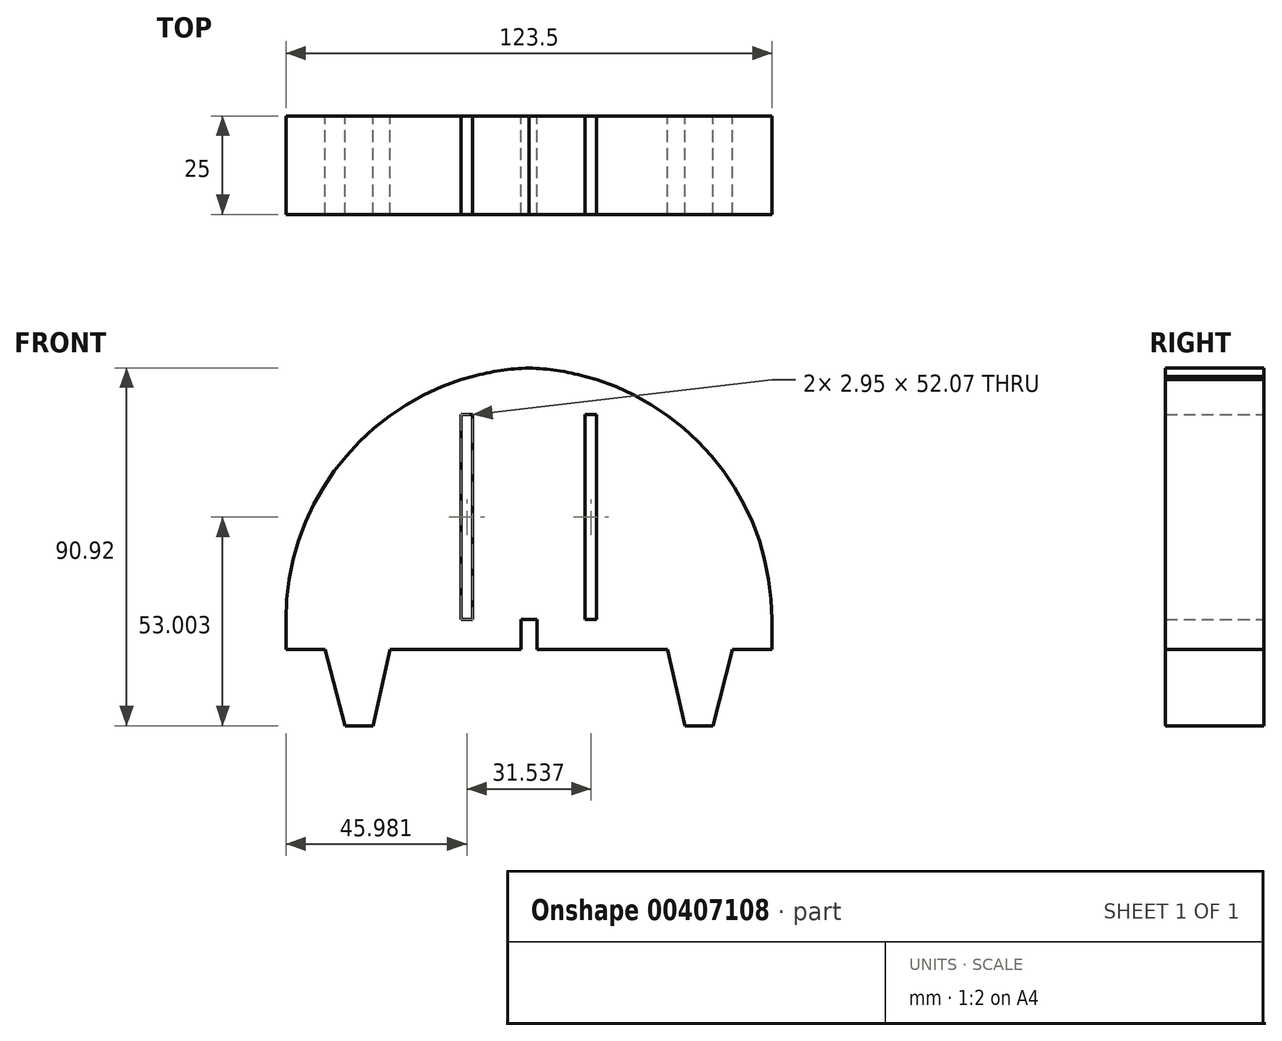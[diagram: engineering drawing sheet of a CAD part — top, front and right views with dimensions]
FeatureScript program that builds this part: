
annotation { "Feature Type Name" : "Feature", "Feature Type Description" : "" }
export const myFeature = defineFeature(function(context is Context, id is Id, definition is map)
    precondition{}
    {
        {
            var Q0;
            Q0=qCreatedBy(makeId("Front.planeOp"),FACE);
            var sketch = newSketch(context, id + "F0", { "sketchPlane" : qUnion([Q0])});
            skArc(sketch, "E0", {"start": v(0, 63.95) * mm, "mid": v(-7.2, 63.29) * mm, "end": v(-14.3, 61.81) * mm});
            skLineSegment(sketch, "E1", {"start": v(-17.24, 0) * mm, "end": v(-14.3, 0) * mm});
            skLineSegment(sketch, "E2.top", {"start": v(-61.75, -7.6) * mm, "end": v(-51.73, -7.6) * mm});
            skLineSegment(sketch, "E3.left", {"start": v(-2.01, 0) * mm, "end": v(-2.01, -7.6) * mm});
            skLineSegment(sketch, "E4.trimOffspring", {"start": v(66, 0) * mm, "end": v(66.22, 0) * mm});
            skLineSegment(sketch, "E5.left", {"start": v(-17.24, 52.07) * mm, "end": v(-17.24, 0) * mm});
            skLineSegment(sketch, "E5.right", {"start": v(-14.3, 52.07) * mm, "end": v(-14.3, 0) * mm});
            skArc(sketch, "E6.trimOffspring", {"start": v(-17.24, 60.95) * mm, "mid": v(-49.44, 37.73) * mm, "end": v(-61.75, 0) * mm});
            skLineSegment(sketch, "E7", {"start": v(-51.73, -7.6) * mm, "end": v(-46.72, -26.97) * mm});
            skLineSegment(sketch, "E8", {"start": v(-46.72, -26.97) * mm, "end": v(-39.64, -26.97) * mm});
            skLineSegment(sketch, "E9", {"start": v(-39.64, -26.97) * mm, "end": v(-35.22, -7.6) * mm});
            skLineSegment(sketch, "E10.trimOffspring", {"start": v(-35.22, -7.6) * mm, "end": v(-2.01, -7.6) * mm});
            skPoint(sketch, "E3.right.end.orphan", {"position": v(2.24, -7.6) * mm});
            skLineSegment(sketch, "E11.MirrorCS", {"start": v(17.24, 0) * mm, "end": v(14.3, 0) * mm});
            skLineSegment(sketch, "E12.MirrorCS", {"start": v(2.01, 0) * mm, "end": v(2.01, -7.6) * mm});
            skLineSegment(sketch, "E13.MirrorCS", {"start": v(46.72, -26.97) * mm, "end": v(39.64, -26.97) * mm});
            skLineSegment(sketch, "E14.MirrorCS", {"start": v(51.73, -7.6) * mm, "end": v(46.72, -26.97) * mm});
            skPoint(sketch, "E15.MirrorP", {"position": v(-2.24, -7.6) * mm});
            skLineSegment(sketch, "E16.MirrorCS", {"start": v(14.3, 52.07) * mm, "end": v(14.3, 0) * mm});
            skLineSegment(sketch, "E17.MirrorCS", {"start": v(61.75, -7.6) * mm, "end": v(51.73, -7.6) * mm});
            skLineSegment(sketch, "E18.MirrorCS", {"start": v(35.22, -7.6) * mm, "end": v(2.01, -7.6) * mm});
            skArc(sketch, "E19.MirrorCS", {"start": v(0, 63.95) * mm, "mid": v(7.2, 63.29) * mm, "end": v(14.3, 61.81) * mm});
            skLineSegment(sketch, "E20.MirrorCS", {"start": v(17.24, 52.07) * mm, "end": v(17.24, 0) * mm});
            skArc(sketch, "E21.MirrorCS", {"start": v(17.24, 60.95) * mm, "mid": v(49.44, 37.73) * mm, "end": v(61.75, 0) * mm});
            skLineSegment(sketch, "E22.MirrorCS", {"start": v(39.64, -26.97) * mm, "end": v(35.22, -7.6) * mm});
            skLineSegment(sketch, "E23", {"start": v(-61.75, -7.6) * mm, "end": v(-61.75, 0) * mm});
            skLineSegment(sketch, "E24", {"start": v(61.75, -7.6) * mm, "end": v(61.75, 0) * mm});
            skLineSegment(sketch, "E25", {"start": v(-17.24, 60.95) * mm, "end": v(-14.3, 61.81) * mm});
            skLineSegment(sketch, "E26", {"start": v(14.3, 61.81) * mm, "end": v(17.24, 60.95) * mm});
            skLineSegment(sketch, "E27", {"start": v(-17.24, 52.07) * mm, "end": v(-14.3, 52.07) * mm});
            skLineSegment(sketch, "E28.trimOffspring", {"start": v(14.3, 52.07) * mm, "end": v(17.24, 52.07) * mm});
            skLineSegment(sketch, "E29.trimOffspring", {"start": v(2.24, 0) * mm, "end": v(2.01, 0) * mm});
            skLineSegment(sketch, "E30.trimOffspring", {"start": v(-2.24, 0) * mm, "end": v(-2.01, 0) * mm});
            skLineSegment(sketch, "E31", {"start": v(2.24, 0) * mm, "end": v(-2.01, 0) * mm});
            skSolve(sketch);
        }
        {
            var Q0;
            {var subQ2=sQuery(id+"F0.wireOp",EDGE,"E5.left");Q0=makeQuery(id+"F0.imprint","IMPRINT",FACE,{"disambiguationData":[TD([[makeQuery(id+"F0.imprint","IMPRINT",EDGE,{"derivedFrom":subQ2}),-1.0]])]});}
            var Q1;
            {var subQ0=sQuery(id+"F0.wireOp",EDGE,"E20.MirrorCS");Q1=makeQuery(id+"F0.imprint","IMPRINT",FACE,{"disambiguationData":[TD([[makeQuery(id+"F0.imprint","IMPRINT",EDGE,{"derivedFrom":subQ0}),1.0]])]});}
            var Q2;
            Q2=makeQuery(id+"F0.imprint","IMPRINT",FACE,{"disambiguationData":[TD([[makeQuery(id+"F0.imprint","IMPRINT",EDGE,{"derivedFrom":sQuery(id+"F0.wireOp",EDGE,"E2.top")}),1.0]])]});
            var Q3;
            {var subQ1=sQuery(id+"F0.wireOp",EDGE,"E12.MirrorCS");Q3=makeQuery(id+"F0.imprint","IMPRINT",FACE,{"disambiguationData":[TD([[makeQuery(id+"F0.imprint","IMPRINT",EDGE,{"derivedFrom":subQ1}),1.0]])]});}
            extrude(context, id + "F1", {"entities" : qUnion([Q0, Q1, Q2, Q3]), "depth" : 25 * mm});
        }
    });
